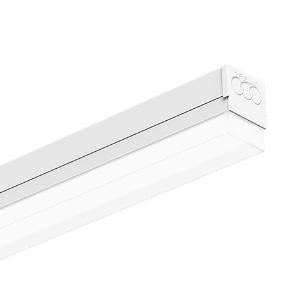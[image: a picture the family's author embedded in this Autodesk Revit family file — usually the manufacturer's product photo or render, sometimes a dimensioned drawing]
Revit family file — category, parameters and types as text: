
# Revit family: 3f_filippi_-_3f_linux_dr_3f_filippi_-_a20526_-_3f_linux_dr_2x22_led_dali_l1778
name_source: partatom
category: Lighting Fixtures
units: mm (PartAtom-declared; Revit-internal decimal feet)

## family parameters
Cut with Voids When Loaded = No
Host = Face
Light Source = No
Part Type = Normal
Room Calculation Point = No
Round Connector Dimension = Use Diameter
Shared = No

## types (1)
- 3F Filippi - 3F Linux DR (1 x LED, 6253 lm, 49 W, 4000 K)
    Apparent Load = 49 VA
    Approval mark = CE
    CIE Flux Codes = 41 72 91 86 100
    Color Rendering = 80
    Color Temperature = 4000 K
    Control Gear = Electronic transformer
    Default Elevation = 1800 mm
    Description = Light unit for structure continues 3F Linux S.

ILLUMINOTECHNICAL
Luminous efficiency 100% (DLOR 86%, ULOR 14%).
Initial luminous flux of the luminaire 6253 lm.
Diffused symmetric distribution.
Installation Interdistance Transv.D = 1.38 x hu - Long.D = 1.25 x hu.
Tabular UGR (CIE 117 - 4H-8H; S=0.25H; 70/50/20): RUG 25 - 23.6.
Beam angle: 136° - 112°.
Luminous efficacy 128 lm/W.
Lifetime (L93/B10): 30000 h. (tq+25°C)
Lifetime (L90/B10): 50000 h. (tq+25°C)
Lifetime (L85/B10): 80000 h. (tq+25°C)
Lifetime (L80/B10): 100000 h. (tq+25°C)
Sudden decreased luminous flux after 50000 hours: 0% (C0).
Photobiological safety in compliance with IEC/TR 62778: RG0 risk exempt, (IEC 62471).
In compliance with IEC/EN 62722-2-1 - IEC/EN 62717 standards.

SOURCE
2 linear LED modules 22W/840.
Energy efficiency class (UE 2019/2020 - UE 2019/2015): D.
CIE 13.3 Colour rendering index: CRI >80 (R9 <50%).
IES TM-30 Fidelity Index: Rf = 84 Rg = 95.
CCT nominal colour temperature 4000 K.
Colour initial tolerance (MacAdam): SDCM 3.

MECHANICAL
Light unit in hot-galvanised steel, painted in white polyester base with fixing springs and retractable safety hooks in stainless steel.
Rectangular screen in self-extinguishing polycarbonate, UV stabilised, opal, with smooth outer surface.
Luminaire with limited surface temperature. - D - (EN 60598-2-24)
Dimensions: 1778x62 mm, height 81 mm. Weight 2.49 kg.
IP40 protection degree.
Mechanical strength to impacts IK06 (1 joule).
Glow-wire test resistance 850°C.

ELECTRICAL
Halogen Free DALI-2 DATI (Parts 251, 252, 253), PUSH-DIM, electronic wiring 230V-50/60Hz, power factor 0.95 at full load, THD <25%, constant output current, SELV, class I, 1 driver, 1 DALI addresse.
Power of the luminaire 49 W.
ENEC - CE.
SAFE FLICKER: PstLM=<1 and SVM=<0.4 (IEC TR 61547-1 and IEC TR 63158), to ensure a more comfortable and safe light.
Luminaire compliant with EN 60598-2-22 for power supply from a centralised emergency system CPSS (Central Power Supply System), not incorporated in the luminaire - high risk areas excluded. The default power and flux are 100% in AC and 15% in DC.
Ambient temperature from 0°C to +35°C.
Temperature class T6 max 85°C.
Connection to the structure with 5-pin plug with phase selection (H05Z-U Halogen Free cable section 0.5 mm² HT90).
Relative humidity UR: <85%.

INSTALLATION
Ceiling / Suspended / Wall.
All accessories dedicated to this product are available on the Catalog and on our website www.3F-Filippi.com.

STRUCTURE
Hot-galvanised wired structure, painted in polyester base white, obtained through rolling process.
Saline-mist resistance equal to 300hrs and damp resistance equal to 700hrs.
Through-wiring 5 or 7 poles with cables H07Z-U Halogen Free section 2.5 mm² HT90, with quick connecting terminal, irreversible, start / end and intermediate power towers.
Linear connecting element in hot galvanised steel already mounted on one end to form continuous channels, only L3556 structures.
A20017 - 3F Linux S 5P L3556, structure with through-wiring 5-pole.
A20019 - 3F Linux S 5P L1778, structure with through-wiring 5-pole.
A20024 - 3F Linux S 7P L3556, structure with through-wiring 7-pole.
A20026 - 3F Linux S 7P L1778, structure with through-wiring 7-pole.

APPLICATIONS
Suitable product for food production plants (HACCP), IFS (Food Version 6), BRC (GSFS Food Version 7).
In commercial environments, exhibition areas, shops and stores.

LIGHT MANAGEMENT
Recommended minimum setting: 10%.
The luminaire, equipped with (DALI-2 DATI) driver, can be controlled manually with 3F Easy Dim technology or automatically/manually with wired or wireless DALI/D2D control systems.
The D2D driver guarantees interoperability with other devices with the same certification by making the following information available:
Device Data (Part 251), Energy Report (Part 252), Diagnosis & Maintenance (Part 253).
In electrical systems without a regulation system (manual or automatic) and DALI bus, a suitable jumper must be made on the DA-DA terminals of the appliance.

WARNING
Luminaire designed for disposal/recycling at end-of-life.
Replaceable (LED only) light source by a professional. Replaceable control gear by a professional.
    Height = 81 mm
    Lamp = 1 x LED
    Lamp Light Flux = 6253 lm
    Lamp Power = 49 W
    Lamp count = 1
    Length = 1778 mm
    Lifetime = 50000 h
    Luminous efficacy = 128 lm/W
    Manufacturer = 3F Filippi
    ModVariant = No
    Model = 3F Filippi - A20526 - 3F Linux DR 2x22 LED DALI L1778
    Mounting Place = Ceiling
    Mounting Type = Pendant
    Number of Poles = 1
    OnlyDefault = Yes
    Power Factor = 1
    Product Name = 3F Filippi - 3F Linux DR
    Product group = pendant luminaire
    ProductGroupID = 9
    Protection Class = Protection class I
    Protection Degree = IP 40
    RLX_Detail_Level = 1
    RLX_Emergency_Light_Flux = 0 lm
    RLX_Emergency_Type = 0
    RLX_Emergency_Type_DB = No
    RlxData = <blob elided: 36261 chars, md5=8dcfb849>
    Socket = socket
    Standby Power = 0 W
    System Light Flux = 6253 lm
    System Power = 49 W
    Type Comments = Product without accessories
    Type Image = 3ffilippi_3f_linux_dr.jpg
    URL = http://relux.com
    VarID = ---
    Voltage = 0 V
    Weight = 0.00 kg
    Width = 62 mm  [stored 0.203412 ft]

note: [stored X ft] marks values corroborated as IEEE doubles in the binary element streams (Revit-internal decimal feet)

## geometry (parser evidence)
native form markers: Blend x4, Sweep x13
no freeform markers — native parametric forms only
